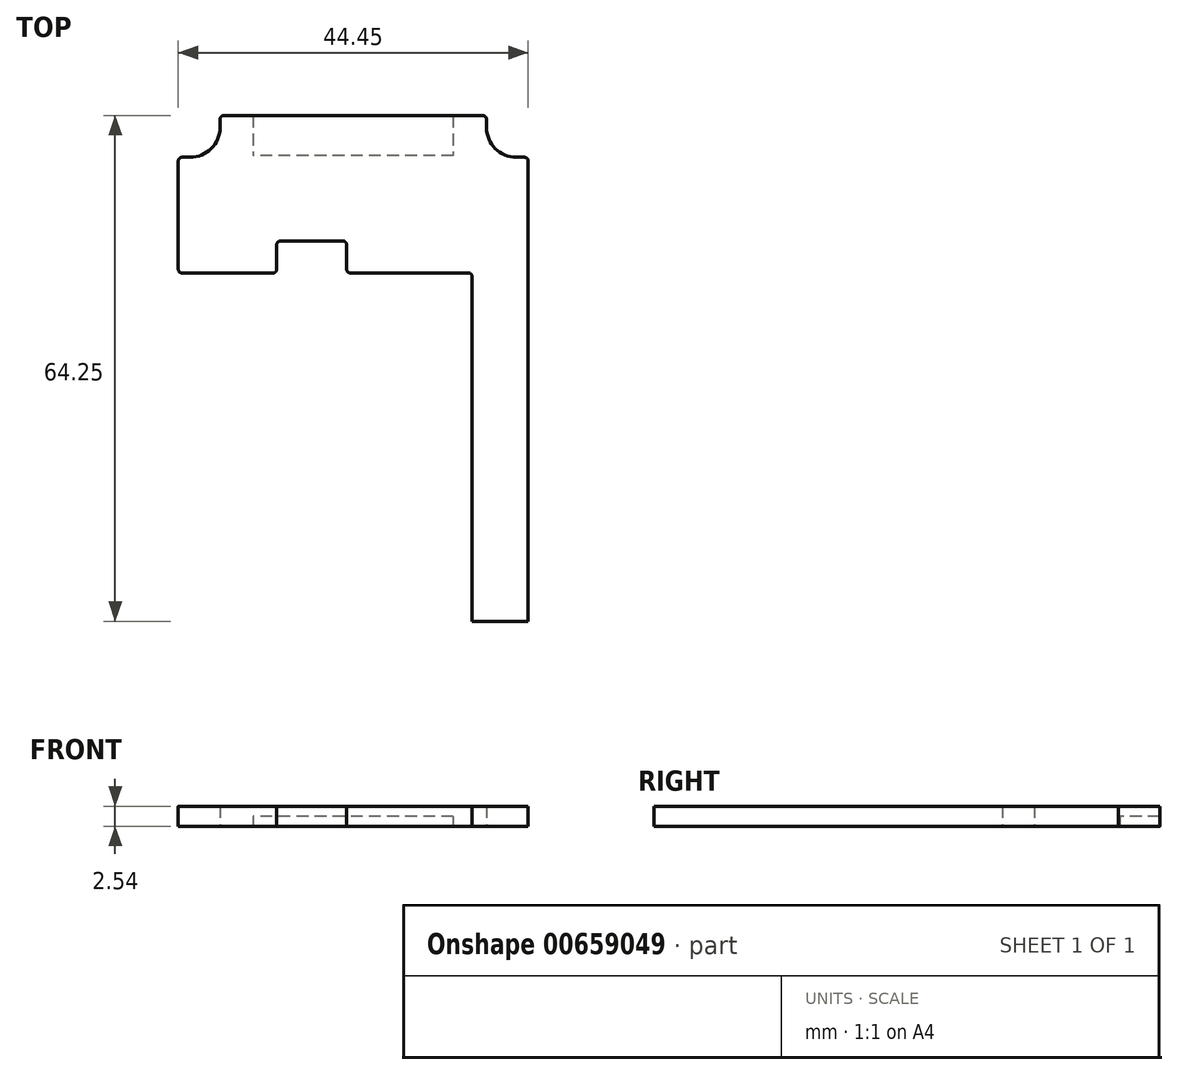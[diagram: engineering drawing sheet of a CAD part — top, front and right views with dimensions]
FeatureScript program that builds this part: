
annotation { "Feature Type Name" : "Feature", "Feature Type Description" : "" }
export const myFeature = defineFeature(function(context is Context, id is Id, definition is map)
    precondition{}
    {
        {
            var Q0;
            Q0=qCreatedBy(makeId("Top.planeOp"),FACE);
            var sketch = newSketch(context, id + "F0", { "sketchPlane" : qUnion([Q0])});
            skLineSegment(sketch, "E0", {"start": v(0, 31.75) * mm, "end": v(0, 75.52) * mm});
            skLineSegment(sketch, "E1", {"start": v(0.48, 0) * mm, "end": v(1.33, 0) * mm, "construction": true});
            skLineSegment(sketch, "E2", {"start": v(7.11, 31.75) * mm, "end": v(7.11, 90.22) * mm});
            skLineSegment(sketch, "E3", {"start": v(1.33, 96) * mm, "end": v(-31.56, 96) * mm});
            skLineSegment(sketch, "E4", {"start": v(-37.34, 90.22) * mm, "end": v(-37.34, 76.48) * mm});
            skLineSegment(sketch, "E5", {"start": v(-36.86, 76) * mm, "end": v(-25.32, 76) * mm});
            skLineSegment(sketch, "E6", {"start": v(1.81, 95.52) * mm, "end": v(1.81, 94.5) * mm});
            skLineSegment(sketch, "E7", {"start": v(5.62, 90.7) * mm, "end": v(6.63, 90.7) * mm});
            skLineSegment(sketch, "E8", {"start": v(-15.11, 96) * mm, "end": v(-15.11, 76) * mm, "construction": true});
            skLineSegment(sketch, "E9.MirrorCS", {"start": v(-35.85, 90.7) * mm, "end": v(-36.86, 90.7) * mm});
            skLineSegment(sketch, "E10.MirrorCS", {"start": v(-32.04, 95.52) * mm, "end": v(-32.04, 94.5) * mm});
            skLineSegment(sketch, "E11", {"start": v(6.63, 5.3) * mm, "end": v(5.62, 5.3) * mm, "construction": true});
            skLineSegment(sketch, "E12", {"start": v(1.81, 1.5) * mm, "end": v(1.81, 0.48) * mm, "construction": true});
            skPoint(sketch, "E13.visualSharp", {"position": v(1.81, 5.3) * mm});
            skArc(sketch, "E13.filletArc", {"start": v(5.62, 5.3) * mm, "mid": v(2.93, 4.18) * mm, "end": v(1.81, 1.5) * mm, "construction": true});
            skPoint(sketch, "E14.orphan", {"position": v(7.11, 96) * mm});
            skPoint(sketch, "E15.orphan", {"position": v(-37.34, 96) * mm});
            skPoint(sketch, "E16.visualSharp", {"position": v(1.81, 90.7) * mm});
            skArc(sketch, "E16.filletArc", {"start": v(1.81, 94.5) * mm, "mid": v(2.93, 91.82) * mm, "end": v(5.62, 90.7) * mm});
            skPoint(sketch, "E17.visualSharp", {"position": v(-32.04, 90.7) * mm});
            skArc(sketch, "E17.filletArc", {"start": v(-35.85, 90.7) * mm, "mid": v(-33.15, 91.82) * mm, "end": v(-32.04, 94.5) * mm});
            skPoint(sketch, "E18.visualSharp", {"position": v(1.81, 96) * mm});
            skArc(sketch, "E18.filletArc", {"start": v(1.81, 95.52) * mm, "mid": v(1.67, 95.86) * mm, "end": v(1.33, 96) * mm});
            skPoint(sketch, "E19.visualSharp", {"position": v(0, 76) * mm});
            skArc(sketch, "E19.filletArc", {"start": v(0, 75.52) * mm, "mid": v(-0.14, 75.86) * mm, "end": v(-0.48, 76) * mm});
            skPoint(sketch, "E20.visualSharp", {"position": v(7.11, 90.7) * mm});
            skArc(sketch, "E20.filletArc", {"start": v(7.11, 90.22) * mm, "mid": v(6.97, 90.56) * mm, "end": v(6.63, 90.7) * mm});
            skPoint(sketch, "E21.visualSharp", {"position": v(-32.04, 96) * mm});
            skArc(sketch, "E21.filletArc", {"start": v(-31.56, 96) * mm, "mid": v(-31.9, 95.86) * mm, "end": v(-32.04, 95.52) * mm});
            skPoint(sketch, "E22.visualSharp", {"position": v(-37.34, 90.7) * mm});
            skArc(sketch, "E22.filletArc", {"start": v(-36.86, 90.7) * mm, "mid": v(-37.2, 90.56) * mm, "end": v(-37.34, 90.22) * mm});
            skPoint(sketch, "E23.visualSharp", {"position": v(-37.34, 76) * mm});
            skArc(sketch, "E23.filletArc", {"start": v(-37.34, 76.48) * mm, "mid": v(-37.2, 76.14) * mm, "end": v(-36.86, 76) * mm});
            skPoint(sketch, "E24.visualSharp", {"position": v(0, 0) * mm});
            skArc(sketch, "E24.filletArc", {"start": v(0, 0.48) * mm, "mid": v(0.14, 0.14) * mm, "end": v(0.48, 0) * mm, "construction": true});
            skPoint(sketch, "E25.visualSharp", {"position": v(1.81, 0) * mm});
            skArc(sketch, "E25.filletArc", {"start": v(1.33, 0) * mm, "mid": v(1.67, 0.14) * mm, "end": v(1.81, 0.48) * mm, "construction": true});
            skPoint(sketch, "E26.visualSharp", {"position": v(7.11, 5.3) * mm});
            skArc(sketch, "E26.filletArc", {"start": v(6.63, 5.3) * mm, "mid": v(6.97, 5.44) * mm, "end": v(7.11, 5.78) * mm, "construction": true});
            skLineSegment(sketch, "E27.top", {"start": v(-24.36, 80.06) * mm, "end": v(-16.43, 80.06) * mm});
            skLineSegment(sketch, "E27.left", {"start": v(-24.84, 76.48) * mm, "end": v(-24.84, 79.59) * mm});
            skLineSegment(sketch, "E27.right", {"start": v(-15.95, 76.48) * mm, "end": v(-15.95, 79.59) * mm});
            skLineSegment(sketch, "E28.trimOffspring", {"start": v(-15.47, 76) * mm, "end": v(-0.48, 76) * mm});
            skLineSegment(sketch, "E29", {"start": v(7.11, 31.75) * mm, "end": v(0, 31.75) * mm});
            skPoint(sketch, "E30.visualSharp", {"position": v(-15.95, 80.06) * mm});
            skArc(sketch, "E30.filletArc", {"start": v(-15.95, 79.59) * mm, "mid": v(-16.09, 79.92) * mm, "end": v(-16.43, 80.06) * mm});
            skPoint(sketch, "E31.visualSharp", {"position": v(-24.84, 80.06) * mm});
            skArc(sketch, "E31.filletArc", {"start": v(-24.36, 80.06) * mm, "mid": v(-24.7, 79.92) * mm, "end": v(-24.84, 79.59) * mm});
            skPoint(sketch, "E32.visualSharp", {"position": v(-24.84, 76) * mm});
            skArc(sketch, "E32.filletArc", {"start": v(-25.32, 76) * mm, "mid": v(-24.98, 76.14) * mm, "end": v(-24.84, 76.48) * mm});
            skPoint(sketch, "E33.visualSharp", {"position": v(-15.95, 76) * mm});
            skArc(sketch, "E33.filletArc", {"start": v(-15.95, 76.48) * mm, "mid": v(-15.8, 76.14) * mm, "end": v(-15.47, 76) * mm});
            skSolve(sketch);
        }
        {
            var Q0;
            Q0=makeQuery(id+"F0.imprint","IMPRINT",FACE,{"disambiguationData":[TD([[makeQuery(id+"F0.imprint","IMPRINT",EDGE,{"derivedFrom":sQuery(id+"F0.wireOp",EDGE,"E0")}),-1.0]])]});
            extrude(context, id + "F1", {"entities" : qUnion([Q0]), "depth" : 2.54 * mm, "offsetDistance" : 25.4 * mm});
        }
        {
            var Q0;
            Q0=makeQuery(id+"F1.opExtrude","CAP_FACE",FACE,{"disambiguationData":[OSD([sQuery(id+"F0.wireOp",EDGE,"E0"),sQuery(id+"F0.wireOp",EDGE,"E2"),sQuery(id+"F0.wireOp",EDGE,"E3"),sQuery(id+"F0.wireOp",EDGE,"E4"),sQuery(id+"F0.wireOp",EDGE,"E5"),sQuery(id+"F0.wireOp",EDGE,"E6"),sQuery(id+"F0.wireOp",EDGE,"E7"),sQuery(id+"F0.wireOp",EDGE,"E9.MirrorCS"),sQuery(id+"F0.wireOp",EDGE,"E10.MirrorCS"),sQuery(id+"F0.wireOp",EDGE,"E16.filletArc"),sQuery(id+"F0.wireOp",EDGE,"E17.filletArc"),sQuery(id+"F0.wireOp",EDGE,"E18.filletArc"),sQuery(id+"F0.wireOp",EDGE,"E19.filletArc"),sQuery(id+"F0.wireOp",EDGE,"E20.filletArc"),sQuery(id+"F0.wireOp",EDGE,"E21.filletArc"),sQuery(id+"F0.wireOp",EDGE,"E22.filletArc"),sQuery(id+"F0.wireOp",EDGE,"E23.filletArc"),sQuery(id+"F0.wireOp",EDGE,"E27.top"),sQuery(id+"F0.wireOp",EDGE,"E27.left"),sQuery(id+"F0.wireOp",EDGE,"E27.right"),sQuery(id+"F0.wireOp",EDGE,"E28.trimOffspring"),sQuery(id+"F0.wireOp",EDGE,"E29"),sQuery(id+"F0.wireOp",EDGE,"E30.filletArc"),sQuery(id+"F0.wireOp",EDGE,"E31.filletArc"),sQuery(id+"F0.wireOp",EDGE,"E32.filletArc"),sQuery(id+"F0.wireOp",EDGE,"E33.filletArc")])],"isStart":true});
            var sketch = newSketch(context, id + "F2", { "sketchPlane" : qUnion([Q0])});
            skLineSegment(sketch, "E34.bottom", {"start": v(-2.41, -96) * mm, "end": v(-27.81, -96) * mm});
            skLineSegment(sketch, "E34.top", {"start": v(-2.41, -90.92) * mm, "end": v(-27.81, -90.92) * mm});
            skLineSegment(sketch, "E34.left", {"start": v(-2.41, -96) * mm, "end": v(-2.41, -90.92) * mm});
            skLineSegment(sketch, "E34.right", {"start": v(-27.81, -96) * mm, "end": v(-27.81, -90.92) * mm});
            skLineSegment(sketch, "E35", {"start": v(-15.11, -96) * mm, "end": v(-15.11, -76) * mm, "construction": true});
            skLineSegment(sketch, "E36", {"start": v(-15.11, -96) * mm, "end": v(-15.11, -90.92) * mm, "construction": true});
            skSolve(sketch);
        }
        {
            var Q0;
            Q0 = qSketchRegion(id + "F2", true);
            extrude(context, id + "F3", {"entities" : qUnion([Q0]), "operationType" : NewBodyOperationType.REMOVE, "oppositeDirection" : true, "depth" : 1.27 * mm, "offsetDistance" : 25.4 * mm});
        }
    });
